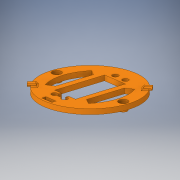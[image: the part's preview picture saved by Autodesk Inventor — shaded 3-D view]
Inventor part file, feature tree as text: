
AUTODESK INVENTOR PART (.ipt)
format: ipt  version: 2018 (Build 220112000, 112)  size: 297,472 bytes
history: native  units: mm
features: extrude x11, sketch x11, mirror x4, fillet x2, pattern_circular x2, projected_geometry x1
ambient origin geometry x8: Origin, YZ Plane, XZ Plane, XY Plane, X Axis, Y Axis, Z Axis, Center Point
bodies: Solid1 (feature_tree)
feature tree (31):
  extrude  "Extrusion1"  Depth=41.6mm
  extrude  "Extrusion2"  Depth=20.8mm
  extrude  "Extrusion3"  Depth=5.0mm
  extrude  "Extrusion4"  Depth=5.0mm
  extrude  "Extrusion5"  Depth=4.0mm
  mirror  "Mirror1"
  extrude  "Extrusion6"  Depth=4.0mm
  mirror  "Mirror2"
  extrude  "Extrusion8"  Depth=4.0mm TaperAngle=0.0deg
  extrude  "Extrusion9"  Depth=2.5mm TaperAngle=0.0deg
  mirror  "Mirror3"
  fillet  "Fillet1"  Radius=6.5mm
  extrude  "Extrusion10"  Depth=4.5mm
  mirror  "Mirror4"
  fillet  "Fillet2"  Radius=5.0mm
  pattern_circular  "Circular Pattern1"  [2 undecoded]
  pattern_circular  "Circular Pattern2"  [2 undecoded]
  extrude  "Extrusion11"  Depth=3.5mm TaperAngle=0.0deg
  extrude  "Extrusion12"  Depth=3.5mm
  sketch  "Sketch1"  dims[d0=20.7mm d1=41.6mm]
  sketch  "Sketch2"  dims[d2=10.35mm d3=20.8mm]
  projected_geometry  "Projected Loop1"
  sketch  "Sketch3"  dims[d4=5.0mm d5=5.0mm]
  sketch  "Sketch4"  dims[d6=5.0mm d7=5.0mm]
  sketch  "Sketch5"  dims[d8=4.0mm d9=0.0mm d10=76.2mm]
  sketch  "Sketch6"  dims[d11=4.0mm d12=0.0mm d13=33.02mm]
  sketch  "Sketch8"  dims[d14=4.85mm d15=4.0mm d16=0.0mm]
  sketch  "Sketch9"  dims[d17=7.5mm d18=2.5mm d19=0.0mm d20=6.5mm]
  sketch  "Sketch10"  dims[d21=2.0mm d22=0.0mm d23=4.5mm d24=5.0mm]
  sketch  "Sketch12"  dims[d25=5.0mm]
  sketch  "Sketch13"  dims[d26=4.5mm d27=10.0mm d28=5.0mm d29=2.0mm d30=0.0mm d36=7.0mm d37=3.5mm d38=5.0mm d39=2.0mm d40=0.0mm d41=5.0mm d42=2.5mm d43=6.0mm d44=2.0mm d45=2.0mm d46=0.0mm d47=1.0mm d49=5.0mm d50=5.0mm d51=5.0mm d52=120.0deg d53=120.0deg d54=7.0mm d55=7.0mm d56=35.0mm d57=2.0mm d58=0.0mm d73=1.0mm d74=20.0mm d75=-7.853982mm d77=20.0mm d78=135.0deg d80=2.0mm d81=0.0mm d82=10.0mm d83=3.5mm d84=5.0mm d85=36.0mm d86=2.0mm d87=0.0mm]
note: 4 required parameter values undecoded (feature->parameter linkage not recoverable at this tier; creation-order binding heuristic only, values carry confidence <= 0.55)
